# Revit family: Power-ModularDevices-GEWISS-90AM-BELL
name_source: partatom
category: Apparecchi elettrici
revit_build: Autodesk Revit 2016 (Build: 20161004_0715(x64)
units: mm (PartAtom-declared; Revit-internal decimal feet)

## family parameters
Condiviso = No
Host = Superficie
Mantenere orientamento annotazione = Sì
Numero OmniClass = 23.80.50.00
Punto di calcolo locali = Sì
Quota connettore circolare = Usa diametro
Taglio con vuoti quando caricato = No
Tipo di parte = Normale
Titolo OmniClass = Terminals for Power Supply

## types (2) — shared parameters
Barra_DIN = 5 mm  [stored 0.0164042 ft]
Catalogue = POWER
Catalogue Range = 90 AM
Electrocod = 140
IDF = 684af0da-83ee-4406-b97d-f9a1985257c7
IDT = dbfca19a-79f5-41ac-b377-066fb2b6a901
Immagine tipo = GW96402.jpg
Numero di poli = 1
Produttore = GEWISS S.p.A.
Prospetto di default = 1219 mm
Spostamento_x = -3000 mm  [stored -9.84252 ft]
Technical sheet = https://www.gewiss.com
URL = https://www.gewiss.com
Version file RFA = 18.0
carico = Altro
potenza in watt = 230 V

## per-type parameters (varying)
| type | Descrizione | EAN code | Modello | No. Chorus modules | No. of modules EN 50022 | Power loss | Rated voltage | SEO |
| GW96401 - BELL 12V AC 1M. | BELL 12V AC 1M. | 8011564063624 | GW96401 | 1 | 1 | 5VA | 12V | Ringer |
| GW96402 - BELL 230V AC 1M. | BELL 230V AC 1M. | 8011564063631 | GW96402 |  |  |  |  |  |

note: [stored X ft] marks values corroborated as IEEE doubles in the binary element streams (Revit-internal decimal feet)
